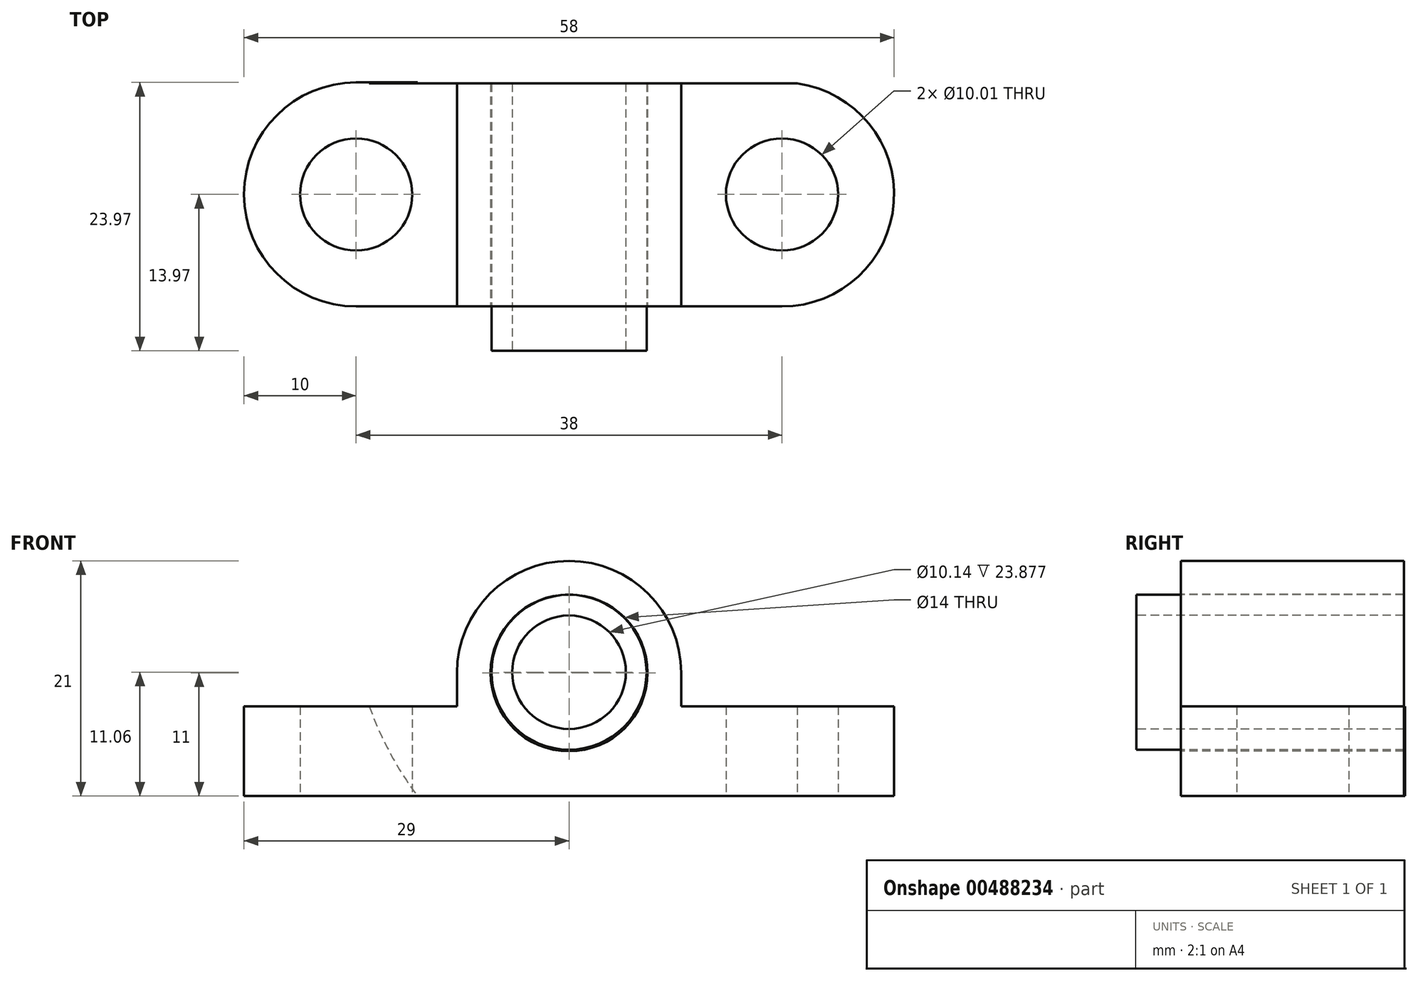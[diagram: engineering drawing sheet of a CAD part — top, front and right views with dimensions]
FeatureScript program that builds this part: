
annotation { "Feature Type Name" : "Feature", "Feature Type Description" : "" }
export const myFeature = defineFeature(function(context is Context, id is Id, definition is map)
    precondition{}
    {
        {
            var Q0;
            Q0=qCreatedBy(makeId("Top.planeOp"),FACE);
            var sketch = newSketch(context, id + "F0", { "sketchPlane" : qUnion([Q0])});
            skLineSegment(sketch, "E0", {"start": v(-19, -10) * mm, "end": v(19, -10) * mm});
            skLineSegment(sketch, "E1", {"start": v(-19, 10) * mm, "end": v(19, 10) * mm});
            skArc(sketch, "E2", {"start": v(19, -10) * mm, "mid": v(29, 0) * mm, "end": v(19, 10) * mm});
            skArc(sketch, "E3", {"start": v(-19, 10) * mm, "mid": v(-29, 0) * mm, "end": v(-19, -10) * mm});
            skCircle(sketch, "E4", {"center": v(19, 0) * mm, "radius": 5 * mm});
            skCircle(sketch, "E5", {"center": v(-19, 0) * mm, "radius": 5 * mm});
            skSolve(sketch);
        }
        {
            var Q0;
            Q0=makeQuery(id+"F0.imprint","IMPRINT",FACE,{"disambiguationData":[TD([[makeQuery(id+"F0.imprint","IMPRINT",EDGE,{"derivedFrom":sQuery(id+"F0.wireOp",EDGE,"E0")}),1.0]])]});
            extrude(context, id + "F1", {"entities" : qUnion([Q0]), "depth" : 8 * mm});
        }
        {
            var Q0;
            Q0=makeQuery(id+"F1.opExtrude","SWEPT_FACE",FACE,{"disambiguationData":[OSD([sQuery(id+"F0.wireOp",EDGE,"E0")])]});
            var sketch = newSketch(context, id + "F2", { "sketchPlane" : qUnion([Q0])});
            skLineSegment(sketch, "E6", {"start": v(10, 8) * mm, "end": v(10, 11) * mm});
            skLineSegment(sketch, "E7", {"start": v(-10, 8) * mm, "end": v(-10, 11) * mm});
            skArc(sketch, "E8", {"start": v(10, 11) * mm, "mid": v(0, 21) * mm, "end": v(-10, 11) * mm});
            skCircle(sketch, "E9", {"center": v(0, 11) * mm, "radius": 7 * mm});
            skCircle(sketch, "E10", {"center": v(0, 11) * mm, "radius": 5 * mm});
            skLineSegment(sketch, "E11", {"start": v(10, 8) * mm, "end": v(10, 0) * mm});
            skLineSegment(sketch, "E12", {"start": v(10, 0) * mm, "end": v(-10, 0) * mm});
            skLineSegment(sketch, "E13", {"start": v(-10, 0) * mm, "end": v(-10, 8) * mm});
            skSolve(sketch);
        }
        {
            var Q0;
            Q0=qCreatedBy(makeId("Front.planeOp"),FACE);
            var sketch = newSketch(context, id + "F3", { "sketchPlane" : qUnion([Q0])});
            skCircle(sketch, "E14", {"center": v(0, 11) * mm, "radius": 7 * mm});
            skSolve(sketch);
        }
        {
            var Q0;
            Q0=makeQuery(id+"F3.imprint","IMPRINT",FACE,{"disambiguationData":[TD([[makeQuery(id+"F3.imprint","IMPRINT",EDGE,{"derivedFrom":sQuery(id+"F3.wireOp",EDGE,"E14")}),1.0]])]});
            extrude(context, id + "F4", {"entities" : qUnion([Q0]), "operationType" : NewBodyOperationType.REMOVE, "endBound" : BoundingType.THROUGH_ALL, "oppositeDirection" : true, "depth" : 12.95 * mm});
        }
        {
            var Q0;
            Q0=makeQuery(id+"F4.boolean.opBoolean","COPY",FACE,{"derivedFrom":makeQuery(id+"F4.opExtrude","CAP_FACE",FACE,{"disambiguationData":[OSD([sQuery(id+"F3.wireOp",EDGE,"E14")])],"isStart":true})});
            extrude(context, id + "F5", {"entities" : qUnion([Q0]), "operationType" : NewBodyOperationType.REMOVE, "oppositeDirection" : true, "depth" : 25.4 * mm});
        }
        {
            var Q0;
            Q0 = qSketchRegion(id + "F2", true);
            extrude(context, id + "F6", {"entities" : qUnion([Q0]), "operationType" : NewBodyOperationType.ADD, "oppositeDirection" : true, "depth" : 20.02 * mm});
        }
        {
            var Q0;
            Q0=makeQuery(id+"F6.opExtrude","CAP_FACE",FACE,{"disambiguationData":[OSD([sQuery(id+"F2.wireOp",EDGE,"E6"),sQuery(id+"F2.wireOp",EDGE,"E7"),sQuery(id+"F2.wireOp",EDGE,"E8"),sQuery(id+"F2.wireOp",EDGE,"E9"),sQuery(id+"F2.wireOp",EDGE,"E11"),sQuery(id+"F2.wireOp",EDGE,"E12"),sQuery(id+"F2.wireOp",EDGE,"E13")])],"isStart":false});
            extrude(context, id + "F7", {"entities" : qUnion([Q0]), "operationType" : NewBodyOperationType.ADD, "depth" : 4 * mm});
        }
        {
            var Q0;
            Q0=qCreatedBy(makeId("Front.planeOp"),FACE);
            var sketch = newSketch(context, id + "F8", { "sketchPlane" : qUnion([Q0])});
            skCircle(sketch, "E15", {"center": v(0, 11.06) * mm, "radius": 6.91 * mm});
            skCircle(sketch, "E16", {"center": v(0, 11.06) * mm, "radius": 5.07 * mm});
            skSolve(sketch);
        }
        {
            var Q0;
            Q0=makeQuery(id+"F8.imprint","IMPRINT",FACE,{"disambiguationData":[TD([[makeQuery(id+"F8.imprint","IMPRINT",EDGE,{"derivedFrom":sQuery(id+"F8.wireOp",EDGE,"E15")}),1.0]])]});
            extrude(context, id + "F9", {"entities" : qUnion([Q0]), "endBound" : BoundingType.SYMMETRIC, "oppositeDirection" : true, "depth" : 27.94 * mm});
        }
        {
            var Q0;
            Q0=qCreatedBy(makeId("Front.planeOp"),FACE);
            cPlane(context, id + "F10", {"entities" : qUnion([Q0]), "cplaneType" : CPlaneType.OFFSET, "offset" : 9.9 * mm, "oppositeDirection" : true, "width" : 152.4 * mm, "height" : 152.4 * mm});
        }
        {
            var Q0;
            Q0=qCreatedBy(id+"F10.planeOp",FACE);
            var sketch = newSketch(context, id + "F11", { "sketchPlane" : qUnion([Q0])});
            skLineSegment(sketch, "E17.bottom", {"start": v(13.17, -2.8) * mm, "end": v(-11.75, -2.8) * mm});
            skLineSegment(sketch, "E17.top", {"start": v(13.17, 25.42) * mm, "end": v(-11.75, 25.42) * mm});
            skLineSegment(sketch, "E17.left", {"start": v(13.17, -2.8) * mm, "end": v(13.17, 25.42) * mm});
            skLineSegment(sketch, "E17.right", {"start": v(-11.75, -2.8) * mm, "end": v(-11.75, 25.42) * mm});
            skSolve(sketch);
        }
        {
            var Q0;
            Q0 = qSketchRegion(id + "F11", true);
            extrude(context, id + "F12", {"entities" : qUnion([Q0]), "operationType" : NewBodyOperationType.REMOVE, "oppositeDirection" : true, "depth" : 25.4 * mm, "offsetDistance" : 25.4 * mm});
        }
        {
            var Q0;
            Q0=qCreatedBy(id+"F10.planeOp",FACE);
            var sketch = newSketch(context, id + "F13", { "sketchPlane" : qUnion([Q0])});
            skCircle(sketch, "E18", {"center": v(11.78, 18.75) * mm, "radius": 31.5 * mm});
            skSolve(sketch);
        }
        {
            var Q0;
            Q0=makeQuery(id+"F13.imprint","IMPRINT",FACE,{"disambiguationData":[TD([[makeQuery(id+"F13.imprint","IMPRINT",EDGE,{"derivedFrom":sQuery(id+"F13.wireOp",EDGE,"E18")}),1.0]])]});
            extrude(context, id + "F14", {"entities" : qUnion([Q0]), "operationType" : NewBodyOperationType.REMOVE, "oppositeDirection" : true, "depth" : 25.4 * mm, "offsetDistance" : 25.4 * mm});
        }
    });
